# Revit family: 44569583(2020)
name_source: partatom
category: Plumbing Fixtures
revit_build: Autodesk Revit 2017 (Build: 20190508_0315(x64)
units: mm (PartAtom-declared; Revit-internal decimal feet)

## family parameters
Always vertical = Yes
Cut with Voids When Loaded = No
OmniClass Number = 23.45.55.00
OmniClass Title = Sanitary Faucets, Wastes
Part Type = Normal
Room Calculation Point = No
Round Connector Dimension = Use Diameter
Shared = No
Work Plane-Based = No

## types (1)
- 44569583 Cover part for shower faucet
    2D/3D/BIM Files URL = http://static.hansa.com
    AssetType = Fixed
    BIMObjectName = 44569583(2020)
    Backflow Prevention EN1717 = EB
    BodyMaterial = Brass
    Brand = Hansa
    Catalog Drawing URL = http://static.hansa.com
    Category = Shower
    Class = Single lever;Trim Kit
    CloseOffRating = 0
    Color = Chrome
    ConvergoRefNr = 0087-2006-0038-FI
    Customs Code = 84818011
    Dimension Drawing URL = http://static.hansa.com
    DurationUnit = Year
    EAN Number = 4057304014819
    EN Standard = EN 817
    FDV Document URL = http://www.hansa.com
    FaucetMainMaterial = Brass
    Features = Single lever;Trim Kit
    Finish = Polished
    FlowCoefficient = 0
    Group = Shower faucets
    IfcExportAs = IfcValveType
    IfcExportType = FAUCET
    Included = Square rosette ;Sleeve;
    Installation Type = Wall mounted for concealed unit
    Installation and Maintenance = http://static.hansa.com
    Lever Handle = Pin lever;;Lever with H+C symbol
    Manufacturer = Hansa
    ManufacturerName = Hansa
    ManufacturerURL = http://www.hansa.com
    Market = INT;DEU;AUT;CHE;BEL;NLD;FRA;CZE;SVK;ITA;ESP
    Material = Brass
    Max. Hot Water Supply = 90 °C
    Mechanical Parts = Non-return valve(s)
    Model = 44569583 Cover part for shower faucet
    ModelReference = 44569583
    NBSDescription = Water supply fittings for baths
    NBSReference = 45-35-70/315
    Name = 44569583 Cover part for shower faucet
    Name_en = 44569583 Cover part for shower faucet
    NominalDepth = 98 mm
    NominalHeight = 106 mm
    NominalWidth = 175 mm  [stored 0.574147 ft]
    Package Weight = 1.12 kg
    Package external Dimensions = 210.0 x 208.0 x 85.0
    Product Code = 44569583
    Product Datasheet = http://www.hansa.com
    Product Family = HANSASTELA
    Product Image URL = http://static.hansa.com
    Product URL = http://static.hansa.com
    Shape = Sculptured
    Shower Parts = Wall connection ellbow
    Size = 175x105x100 mm
    Spare Parts = http://static.hansa.com
    Technical DataSheet URL = http://www.hansa.com
    Uniclass2 = Pr_40_30_96_78
    Uniclass2015Description = Shower manual water supply sets
    Uniclass2015Reference = Pr_40_20_87_78
    Version = 1
    VersionDate = 06/07/2020
    WarrantyDescription = http://warranty.hansa.com
    WarrantyDurationUnit = Year
    WorkingPressure = 50 - 1000 kPa

note: [stored X ft] marks values corroborated as IEEE doubles in the binary element streams (Revit-internal decimal feet)

## geometry (parser evidence)
native form markers: Sweep x7
no freeform markers — native parametric forms only
